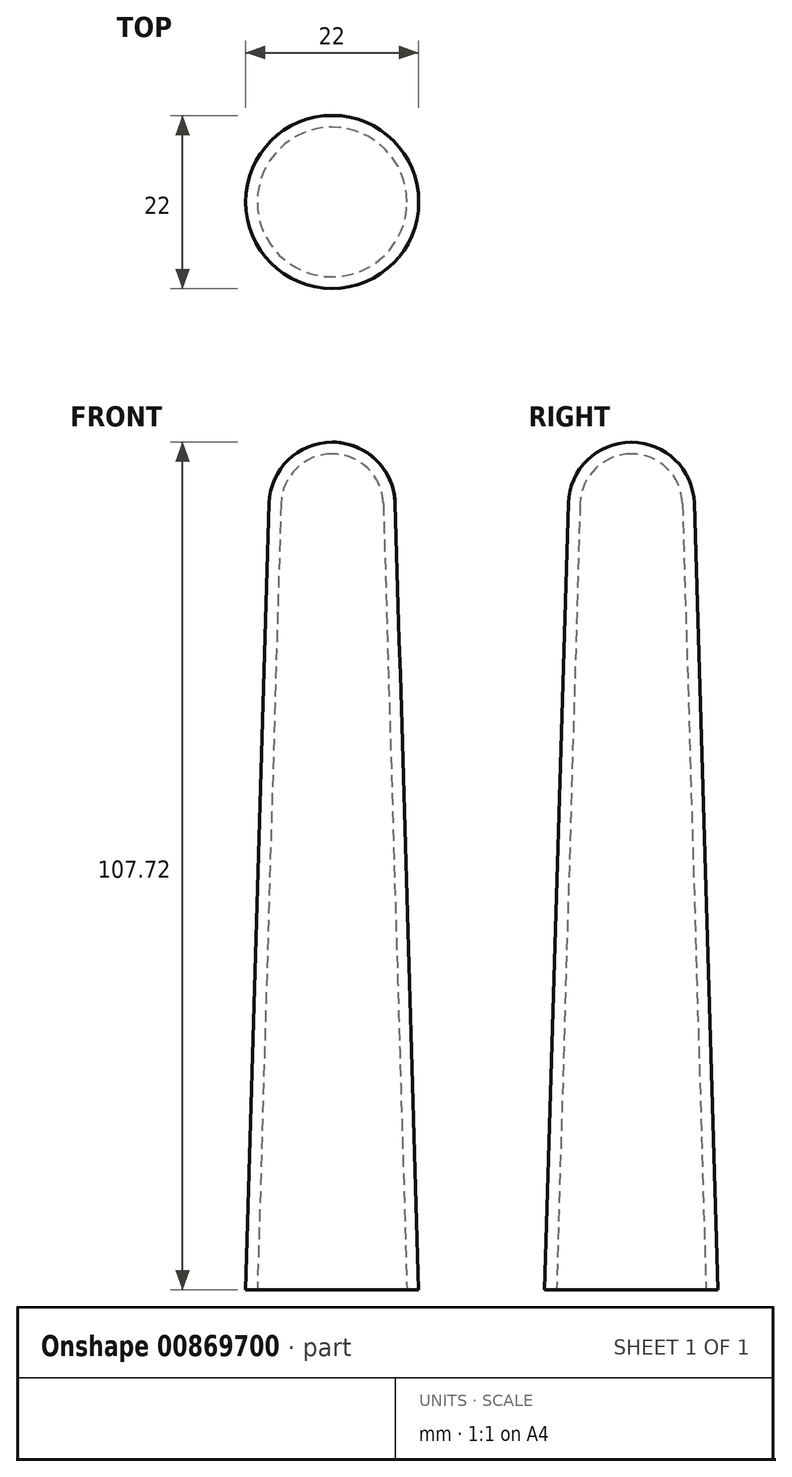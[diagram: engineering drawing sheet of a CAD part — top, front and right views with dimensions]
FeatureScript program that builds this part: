
annotation { "Feature Type Name" : "Feature", "Feature Type Description" : "" }
export const myFeature = defineFeature(function(context is Context, id is Id, definition is map)
    precondition{}
    {
        {
            var Q0;
            Q0=qCreatedBy(makeId("Front.planeOp"),FACE);
            var sketch = newSketch(context, id + "F0", { "sketchPlane" : qUnion([Q0])});
            skLineSegment(sketch, "E0", {"start": v(-8, 69.2) * mm, "end": v(-11, -30.76) * mm});
            skLineSegment(sketch, "E1", {"start": v(-11, -30.76) * mm, "end": v(-9.5, -30.76) * mm});
            skLineSegment(sketch, "E2", {"start": v(-9.5, -30.76) * mm, "end": v(-6.5, 69.15) * mm});
            skArc(sketch, "E3", {"start": v(0, 76.96) * mm, "mid": v(-5.57, 74.7) * mm, "end": v(-8, 69.2) * mm});
            skArc(sketch, "E4", {"start": v(0, 75.46) * mm, "mid": v(-4.53, 73.62) * mm, "end": v(-6.5, 69.15) * mm});
            skLineSegment(sketch, "E5", {"start": v(0, 76.96) * mm, "end": v(0, 75.46) * mm});
            skSolve(sketch);
        }
        {
            var Q0;
            Q0=makeQuery(id+"F0.imprint","IMPRINT",FACE,{"disambiguationData":[TD([[makeQuery(id+"F0.imprint","IMPRINT",EDGE,{"derivedFrom":sQuery(id+"F0.wireOp",EDGE,"E0")}),1.0]])]});
            var Q1;
            Q1=sQuery(id+"F0.wireOp",EDGE,"E5");
            revolve(context, id + "F1", {"surfaceOperationType" : NewSurfaceOperationType.NEW, "entities" : qUnion([Q0]), "axis" : qUnion([Q1]), "revolveType" : RevolveType.FULL});
        }
    });
